FCSTD DOCUMENT  (FreeCAD 1.0R39319 (Git))
Label: week2 sketch 1Unnamed
License: All rights reserved
LicenseURL: https://en.wikipedia.org/wiki/All_rights_reserved
objects: Sketcher::SketchObject×1, PartDesign::Body×1
note: 3 computed .brp shape members not serialized (recipe doc carries the construction recipe); baked Part::Feature solids carry a one-line shape summary decoded from their .brp

FEATURE [Sketcher::SketchObject] Sketch
  ArcFitTolerance = 1e-06
  AttachmentSupport = -> [XY_Plane]
  FullyConstrained = true
  MakeInternals = false
  MapMode = 5
  sketch-geometry (44):
    g0: LineSegment StartX=0 StartY=0 StartZ=0 EndX=-25 EndY=0 EndZ=0
    g1: LineSegment StartX=-25 StartY=0 StartZ=0 EndX=-25 EndY=30 EndZ=0
    g2: LineSegment StartX=-25 StartY=30 StartZ=0 EndX=-16.25 EndY=30 EndZ=0
    g3: LineSegment StartX=-16.25 StartY=30 StartZ=0 EndX=-16.25 EndY=14 EndZ=0
    g4: LineSegment StartX=-16.25 StartY=14 StartZ=0 EndX=-20.75 EndY=14 EndZ=0
    g5: LineSegment StartX=-20.75 StartY=14 StartZ=0 EndX=-20.75 EndY=9.5 EndZ=0
    g6: LineSegment StartX=-20.75 StartY=9.5 StartZ=0 EndX=-8.1 EndY=9.5 EndZ=0
    g7: LineSegment StartX=-8.1 StartY=9.5 StartZ=0 EndX=-8.1 EndY=16.77 EndZ=0
    g8: LineSegment StartX=-8.1 StartY=16.77 StartZ=0 EndX=-3.15 EndY=22.6 EndZ=0
    g9: LineSegment StartX=-3.15 StartY=22.6 StartZ=0 EndX=3.15 EndY=22.6 EndZ=0
    g10: LineSegment StartX=25 StartY=0 StartZ=0 EndX=25 EndY=30 EndZ=0
    g11: LineSegment StartX=25 StartY=30 StartZ=0 EndX=16.25 EndY=30 EndZ=0
    g12: LineSegment StartX=16.25 StartY=30 StartZ=0 EndX=16.25 EndY=14 EndZ=0
    g13: LineSegment StartX=20.75 StartY=14 StartZ=0 EndX=20.75 EndY=9.5 EndZ=0
    g14: LineSegment StartX=16.25 StartY=14 StartZ=0 EndX=20.75 EndY=14 EndZ=0
    g15: LineSegment StartX=20.75 StartY=9.5 StartZ=0 EndX=8.1 EndY=9.5 EndZ=0
    g16: LineSegment StartX=8.1 StartY=16.77 StartZ=0 EndX=3.15 EndY=22.6 EndZ=0
    g17: LineSegment StartX=8.1 StartY=16.77 StartZ=0 EndX=8.1 EndY=9.5 EndZ=0
    g18: LineSegment StartX=0 StartY=0 StartZ=0 EndX=25 EndY=0 EndZ=0
    g19: LineSegment StartX=-44 StartY=8.20559 StartZ=0 EndX=-30 EndY=6.33606 EndZ=0
    g20: LineSegment StartX=-30 StartY=6.33606 StartZ=0 EndX=-30 EndY=22.3361 EndZ=0
    g21: LineSegment StartX=-30 StartY=22.3361 StartZ=0 EndX=-44 EndY=20.4665 EndZ=0
    g22: ArcOfCircle CenterX=-27.4715 CenterY=21.5151 CenterZ=0 NormalX=0 NormalY=0 NormalZ=1 AngleXU=0 Radius=3 StartAngle=3.70988 EndAngle=5.68054
    g23: ArcOfCircle CenterX=-27.535 CenterY=7.51519 CenterZ=0 NormalX=0 NormalY=0 NormalZ=1 AngleXU=0 Radius=3 StartAngle=0.56425 EndAngle=2.53514
    g24: LineSegment StartX=30 StartY=22.3361 StartZ=0 EndX=44 EndY=20.4665 EndZ=0
    g25: LineSegment StartX=44 StartY=8.20559 StartZ=0 EndX=30 EndY=6.33606 EndZ=0
    g26: LineSegment StartX=30 StartY=6.33606 StartZ=0 EndX=30 EndY=22.3361 EndZ=0
    g27: ArcOfCircle CenterX=27.4715 CenterY=21.5151 CenterZ=0 NormalX=0 NormalY=0 NormalZ=1 AngleXU=0 Radius=3 StartAngle=3.74423 EndAngle=5.7149
    g28: ArcOfCircle CenterX=27.535 CenterY=7.51519 CenterZ=0 NormalX=0 NormalY=0 NormalZ=1 AngleXU=0 Radius=3 StartAngle=0.60645 EndAngle=2.57734
    g29: LineSegment StartX=-44 StartY=20.4665 StartZ=0 EndX=-44 EndY=8.20559 EndZ=0
    g30: LineSegment StartX=44 StartY=20.4665 StartZ=0 EndX=44 EndY=8.20652 EndZ=0
    g31: LineSegment StartX=-14.9403 StartY=0 StartZ=0 EndX=-14.9403 EndY=-8.97 EndZ=0
    g32: LineSegment StartX=-14.9403 StartY=-8.97 StartZ=0 EndX=-1.94025 EndY=-8.97 EndZ=0
    g33: LineSegment StartX=-14.9403 StartY=-8.97 StartZ=0 EndX=-13.9593 EndY=-10.7129 EndZ=0
    g34: LineSegment StartX=-13.9593 StartY=-10.7129 StartZ=0 EndX=-1.94025 EndY=-10.7129 EndZ=0
    g35: LineSegment StartX=-1.94025 StartY=-10.7129 StartZ=0 EndX=-1.94025 EndY=-8.97 EndZ=0
    g36: LineSegment StartX=-1.94025 StartY=-8.97 StartZ=0 EndX=-1.94025 EndY=-4.51222 EndZ=0
    g37: LineSegment StartX=15.0597 StartY=-8.8399 StartZ=0 EndX=2.05975 EndY=-8.8399 EndZ=0
    g38: LineSegment StartX=15.0597 StartY=-8.8399 StartZ=0 EndX=14.0788 EndY=-10.5828 EndZ=0
    g39: LineSegment StartX=14.0788 StartY=-10.5828 StartZ=0 EndX=2.05975 EndY=-10.5828 EndZ=0
    g40: LineSegment StartX=2.05975 StartY=-10.5828 StartZ=0 EndX=2.05975 EndY=-8.8399 EndZ=0
    g41: LineSegment StartX=2.05975 StartY=-8.8399 StartZ=0 EndX=2.05975 EndY=-4.51222 EndZ=0
    g42: LineSegment StartX=15.0597 StartY=0.130097 StartZ=0 EndX=15.0597 EndY=-8.8399 EndZ=0
    g43: ArcOfCircle CenterX=0.0597496 CenterY=-4.51222 CenterZ=0 NormalX=0 NormalY=0 NormalZ=1 AngleXU=0 Radius=2 StartAngle=2.46426e-09 EndAngle=3.14159
  constraints (128):
    c: Coincident(g-1,g0)
    c: PointOnObject(g0,g-1)
    c: Coincident(g0,g1)
    c: Vertical(g1)
    c: Coincident(g1,g2)
    c: Horizontal(g2)
    c: Coincident(g2,g3)
    c: Vertical(g3)
    c: Coincident(g3,g4)
    c: Horizontal(g4)
    c: Coincident(g4,g5)
    c: Coincident(g5,g6)
    c: Horizontal(g6)
    c: Coincident(g6,g7)
    c: Coincident(g7,g8)
    c: Coincident(g8,g9)
    c: Horizontal(g9)
    c: DistanceY(g1,g1) = 30
    c: DistanceY(g3,g3) = 16
    c: Distance(g6,g0) = 9.5
    c: Vertical(g5)
    c: Distance(g0,g9) = 22.6
    c: Vertical(g10)
    c: Coincident(g10,g11)
    c: Horizontal(g11)
    c: Coincident(g11,g12)
    c: Vertical(g12)
    c: Coincident(g12,g14)
    c: Horizontal(g14)
    c: Coincident(g14,g13)
    c: Coincident(g13,g15)
    c: Horizontal(g15)
    c: Vertical(g13)
    c: Vertical(g7)
    c: Coincident(g16,g9)
    c: Distance(g10,g1) = 50
    c: Distance(g12,g3) = 32.5
    c: Coincident(g16,g17)
    c: Vertical(g17)
    c: Coincident(g17,g15)
    c: Distance(g17,g7) = 16.2
    c: DistanceX(g9,g9) = 6.3
    c: Equal(g16,g8)
    c: Distance(g9,g15) = 13.1
    c: Distance(g11,g15) = 20.5
    c: Equal(g4,g14)
    c: Equal(g6,g15)
    c: Equal(g17,g7)
    c: Equal(g11,g2)
    c: Coincident(g0,g18)
    c: Coincident(g18,g10)
    c: Horizontal(g18)
    c: Equal(g18,g0)
    c: Equal(g3,g12)
    c: DistanceX(g4,g4) = 4.5
    c: DistanceY(g7,g7) = 7.27
    c: Coincident(g19,g20)
    c: Vertical(g20)
    c: Coincident(g20,g21)
    c: DistanceY(g20,g20) = 16
    c: DistanceX(g19,g19) = 14
    c: Equal(g19,g21)
    c: PointOnObject(g22,g20)
    c: PointOnObject(g23,g20)
    c: PointOnObject(g22,g1)
    c: PointOnObject(g23,g1)
    c: Radius(g23) = 3
    c: Equal(g22,g23)
    c: Distance(g1,g20) = 5
    c: Distance(g22,g23) = 8
    c: Block(g20)
    c: Block(g21)
    c: Block(g19)
    c: Block(g23)
    c: Block(g22)
    c: Coincident(g25,g26)
    c: Vertical(g26)
    c: Coincident(g26,g24)
    c: Equal(g25,g24)
    c: PointOnObject(g27,g26)
    c: Block(g26)
    c: Block(g24)
    c: Block(g25)
    c: Block(g27)
    c: Radius(g28) = 3
    c: Block(g28)
    c: Coincident(g21,g29)
    c: Coincident(g29,g19)
    c: Vertical(g29)
    c: Coincident(g24,g30)
    c: Vertical(g30)
    c: DistanceY(g30,g30) = 12.26
    c: PointOnObject(g31,g0)
    c: Vertical(g31)
    c: Coincident(g31,g32)
    c: Coincident(g31,g33)
    c: Coincident(g33,g34)
    c: Horizontal(g32)
    c: Horizontal(g34)
    c: Distance(g33,g33) = 2
    c: Coincident(g34,g35)
    c: Coincident(g35,g32)
    c: Vertical(g35)
    c: Coincident(g35,g36)
    c: Vertical(g36)
    c: Vertical(g42)
    c: Coincident(g42,g37)
    c: Coincident(g42,g38)
    c: Coincident(g38,g39)
    c: Horizontal(g37)
    c: Horizontal(g39)
    c: Distance(g38,g38) = 2
    c: Coincident(g39,g40)
    c: Coincident(g40,g37)
    c: Vertical(g40)
    c: Coincident(g40,g41)
    c: Vertical(g41)
    c: Distance(g42,g31) = 30
    c: Distance(g40,g35) = 4
    c: Equal(g37,g32)
    c: Diameter(g43) = 4
    c: Coincident(g43,g36)
    c: Coincident(g43,g41)
    c: Equal(g34,g39)
    c: Equal(g31,g42)
    c: DistanceY(g31,g31) = 8.97
    c: Block(g38)
    c: Block(g43)
FEATURE [PartDesign::Body] Body
  AllowCompound = false
  Group = -> [Sketch]
  Origin = -> Origin
